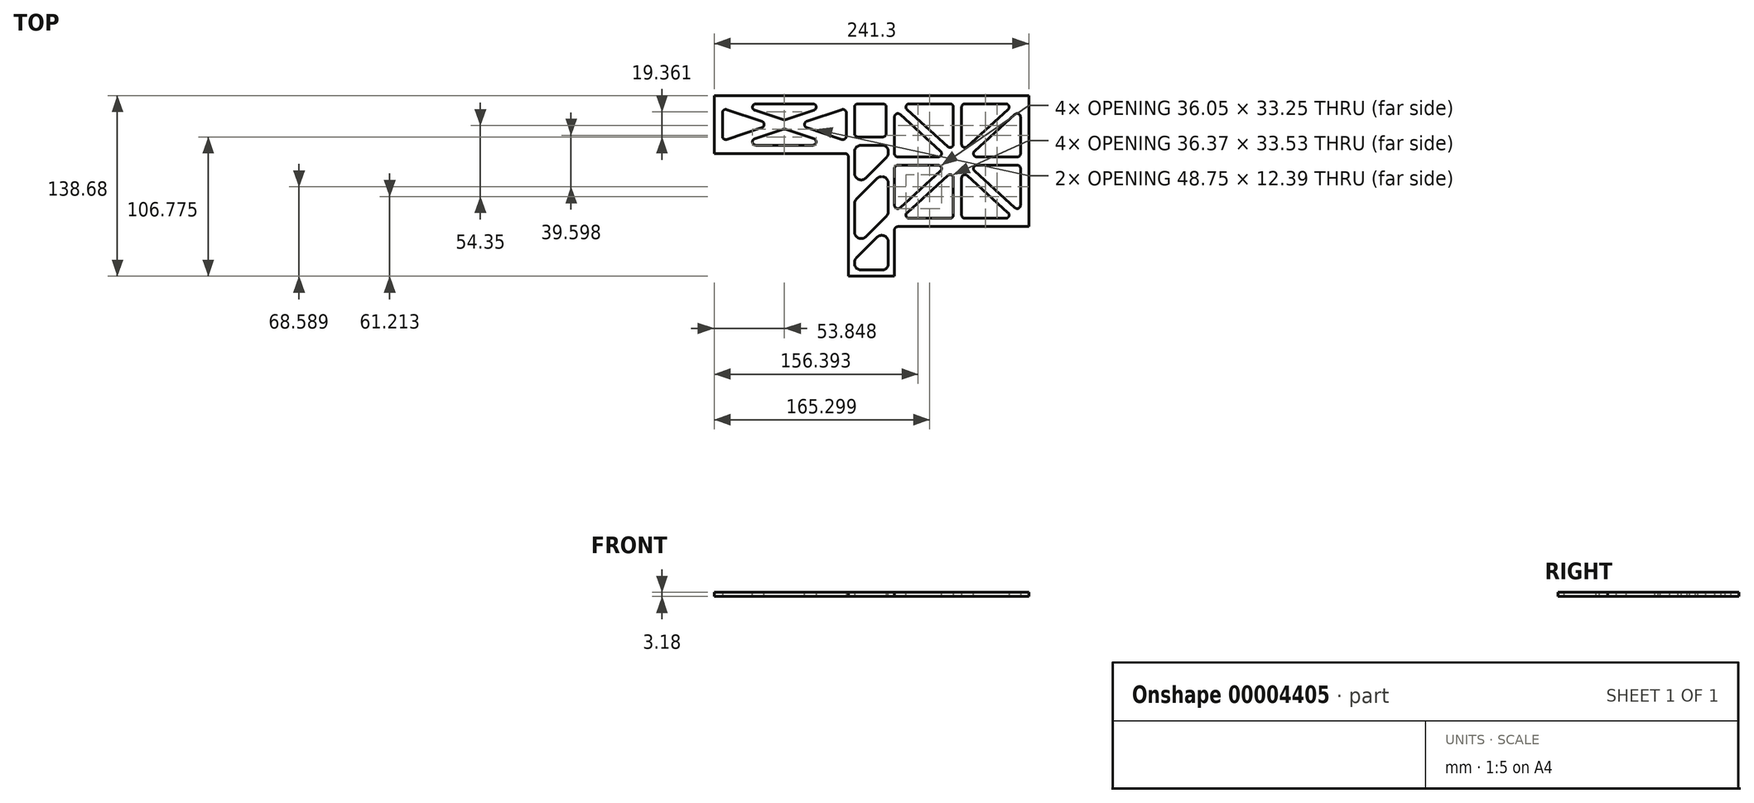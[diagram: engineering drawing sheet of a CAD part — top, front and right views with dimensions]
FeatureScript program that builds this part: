
annotation { "Feature Type Name" : "Feature", "Feature Type Description" : "" }
export const myFeature = defineFeature(function(context is Context, id is Id, definition is map)
    precondition{}
    {
        {
            var Q0;
            Q0=qCreatedBy(makeId("Top.planeOp"),FACE);
            var sketch = newSketch(context, id + "F0", { "sketchPlane" : qUnion([Q0])});
            skLineSegment(sketch, "E0", {"start": v(0, 0) * mm, "end": v(241.3, 0) * mm});
            skLineSegment(sketch, "E1", {"start": v(241.3, 0) * mm, "end": v(241.3, -100.58) * mm});
            skLineSegment(sketch, "E2", {"start": v(241.3, -100.58) * mm, "end": v(138.37, -100.58) * mm});
            skLineSegment(sketch, "E3", {"start": v(102.93, -44.45) * mm, "end": v(0, -44.45) * mm});
            skLineSegment(sketch, "E4", {"start": v(0, -44.45) * mm, "end": v(0, 0) * mm});
            skLineSegment(sketch, "E5.0", {"start": v(6.35, -34.75) * mm, "end": v(6.35, -9.7) * mm});
            skLineSegment(sketch, "E5.1", {"start": v(91.33, -38.1) * mm, "end": v(16.37, -38.1) * mm});
            skLineSegment(sketch, "E5.3", {"start": v(230.23, -94.23) * mm, "end": v(189.83, -94.23) * mm});
            skLineSegment(sketch, "E5.4", {"start": v(234.95, -10.64) * mm, "end": v(234.95, -47.12) * mm});
            skLineSegment(sketch, "E5.5", {"start": v(16.37, -6.35) * mm, "end": v(91.33, -6.35) * mm});
            skLineSegment(sketch, "E6", {"start": v(107.7, -31.75) * mm, "end": v(107.7, -6.35) * mm});
            skLineSegment(sketch, "E7.0", {"start": v(138.37, -89.94) * mm, "end": v(138.37, -53.47) * mm});
            skLineSegment(sketch, "E8.0", {"start": v(101.35, -34.75) * mm, "end": v(101.35, -9.7) * mm});
            skLineSegment(sketch, "E9.trimOffspring", {"start": v(143.08, -6.35) * mm, "end": v(183.48, -6.35) * mm});
            skLineSegment(sketch, "E10.trimOffspring", {"start": v(107.7, -6.35) * mm, "end": v(132.02, -6.35) * mm});
            skLineSegment(sketch, "E11.0", {"start": v(107.7, -31.75) * mm, "end": v(132.02, -31.75) * mm});
            skLineSegment(sketch, "E12.trimOffspring", {"start": v(132.02, -31.75) * mm, "end": v(132.02, -6.35) * mm});
            skLineSegment(sketch, "E13", {"start": v(234.95, -94.23) * mm, "end": v(138.37, -6.35) * mm, "construction": true});
            skLineSegment(sketch, "E14", {"start": v(138.37, -94.23) * mm, "end": v(234.95, -6.35) * mm, "construction": true});
            skLineSegment(sketch, "E15.0", {"start": v(234.95, -89.94) * mm, "end": v(194.87, -53.47) * mm});
            skLineSegment(sketch, "E16.0", {"start": v(230.23, -94.23) * mm, "end": v(189.83, -57.47) * mm});
            skLineSegment(sketch, "E17.0", {"start": v(143.08, -94.23) * mm, "end": v(183.48, -57.47) * mm});
            skLineSegment(sketch, "E18.0", {"start": v(138.37, -89.94) * mm, "end": v(178.45, -53.47) * mm});
            skLineSegment(sketch, "E19.trimOffspring", {"start": v(183.48, -43.11) * mm, "end": v(143.08, -6.35) * mm});
            skLineSegment(sketch, "E20.trimOffspring", {"start": v(194.87, -47.12) * mm, "end": v(234.95, -10.64) * mm});
            skLineSegment(sketch, "E21.trimOffspring", {"start": v(178.45, -47.12) * mm, "end": v(138.37, -10.64) * mm});
            skLineSegment(sketch, "E22.trimOffspring", {"start": v(189.83, -43.11) * mm, "end": v(230.23, -6.35) * mm});
            skLineSegment(sketch, "E23", {"start": v(234.95, -50.3) * mm, "end": v(138.37, -50.3) * mm, "construction": true});
            skLineSegment(sketch, "E24", {"start": v(186.66, -94.23) * mm, "end": v(186.66, -6.35) * mm, "construction": true});
            skLineSegment(sketch, "E25.0", {"start": v(189.83, -94.23) * mm, "end": v(189.83, -57.47) * mm});
            skLineSegment(sketch, "E26.0", {"start": v(183.48, -94.23) * mm, "end": v(183.48, -57.47) * mm});
            skLineSegment(sketch, "E27.0", {"start": v(234.95, -47.12) * mm, "end": v(194.87, -47.12) * mm});
            skLineSegment(sketch, "E28.0", {"start": v(234.95, -53.47) * mm, "end": v(194.87, -53.47) * mm});
            skLineSegment(sketch, "E29.trimOffspring", {"start": v(189.83, -43.11) * mm, "end": v(189.83, -6.35) * mm});
            skLineSegment(sketch, "E30.trimOffspring", {"start": v(183.48, -43.11) * mm, "end": v(183.48, -6.35) * mm});
            skLineSegment(sketch, "E31.trimOffspring", {"start": v(178.45, -47.12) * mm, "end": v(138.37, -47.12) * mm});
            skLineSegment(sketch, "E32.trimOffspring", {"start": v(178.45, -53.47) * mm, "end": v(138.37, -53.47) * mm});
            skLineSegment(sketch, "E33.trimOffspring", {"start": v(183.48, -94.23) * mm, "end": v(143.08, -94.23) * mm});
            skLineSegment(sketch, "E34.trimOffspring", {"start": v(138.37, -47.12) * mm, "end": v(138.37, -10.64) * mm});
            skLineSegment(sketch, "E35.trimOffspring", {"start": v(189.83, -6.35) * mm, "end": v(230.23, -6.35) * mm});
            skLineSegment(sketch, "E36.trimOffspring", {"start": v(234.95, -53.47) * mm, "end": v(234.95, -89.94) * mm});
            skLineSegment(sketch, "E37", {"start": v(101.35, -38.1) * mm, "end": v(6.35, -6.35) * mm, "construction": true});
            skLineSegment(sketch, "E38", {"start": v(6.35, -38.1) * mm, "end": v(101.35, -6.35) * mm, "construction": true});
            skLineSegment(sketch, "E39.0", {"start": v(101.35, -34.75) * mm, "end": v(63.86, -22.23) * mm});
            skLineSegment(sketch, "E40.0", {"start": v(91.33, -38.1) * mm, "end": v(53.85, -25.57) * mm});
            skLineSegment(sketch, "E41.0", {"start": v(16.37, -38.1) * mm, "end": v(53.85, -25.57) * mm});
            skLineSegment(sketch, "E42.0", {"start": v(6.35, -34.75) * mm, "end": v(43.83, -22.23) * mm});
            skLineSegment(sketch, "E43.trimOffspring", {"start": v(53.85, -18.88) * mm, "end": v(16.37, -6.35) * mm});
            skLineSegment(sketch, "E44.trimOffspring", {"start": v(63.86, -22.23) * mm, "end": v(101.35, -9.7) * mm});
            skLineSegment(sketch, "E45.trimOffspring", {"start": v(43.83, -22.23) * mm, "end": v(6.35, -9.7) * mm});
            skLineSegment(sketch, "E46.trimOffspring", {"start": v(53.85, -18.88) * mm, "end": v(91.33, -6.35) * mm});
            skLineSegment(sketch, "E47", {"start": v(138.37, -100.58) * mm, "end": v(138.37, -138.68) * mm});
            skLineSegment(sketch, "E48", {"start": v(138.37, -138.68) * mm, "end": v(102.93, -138.68) * mm});
            skLineSegment(sketch, "E49", {"start": v(102.93, -138.68) * mm, "end": v(102.93, -44.45) * mm});
            skSolve(sketch);
        }
        {
            var Q0;
            Q0=makeQuery(id+"F0.imprint","IMPRINT",FACE,{"disambiguationData":[TD([[makeQuery(id+"F0.imprint","IMPRINT",EDGE,{"derivedFrom":sQuery(id+"F0.wireOp",EDGE,"E0")}),-1.0]])]});
            extrude(context, id + "F1", {"entities" : qUnion([Q0]), "depth" : 3.17 * mm});
        }
        {
            var Q0;
            Q0=makeQuery(id+"F1.opExtrude","SWEPT_EDGE",EDGE,{"disambiguationData":[OSD([sQuery(id+"F0.wireOp",EDGE,"E3"),sQuery(id+"F0.wireOp",EDGE,"E49")])]});
            var Q1;
            Q1=makeQuery(id+"F1.opExtrude","SWEPT_EDGE",EDGE,{"disambiguationData":[OSD([sQuery(id+"F0.wireOp",EDGE,"E15.0"),sQuery(id+"F0.wireOp",EDGE,"E36.trimOffspring")])]});
            var Q2;
            Q2=makeQuery(id+"F1.opExtrude","SWEPT_EDGE",EDGE,{"disambiguationData":[OSD([sQuery(id+"F0.wireOp",EDGE,"E26.0"),sQuery(id+"F0.wireOp",EDGE,"E33.trimOffspring")])]});
            var Q3;
            Q3=makeQuery(id+"F1.opExtrude","SWEPT_EDGE",EDGE,{"disambiguationData":[OSD([sQuery(id+"F0.wireOp",EDGE,"E19.trimOffspring"),sQuery(id+"F0.wireOp",EDGE,"E30.trimOffspring")])]});
            var Q4;
            Q4=makeQuery(id+"F1.opExtrude","SWEPT_EDGE",EDGE,{"disambiguationData":[OSD([sQuery(id+"F0.wireOp",EDGE,"E5.4"),sQuery(id+"F0.wireOp",EDGE,"E27.0")])]});
            var Q5;
            Q5=makeQuery(id+"F1.opExtrude","SWEPT_EDGE",EDGE,{"disambiguationData":[OSD([sQuery(id+"F0.wireOp",EDGE,"E11.0"),sQuery(id+"F0.wireOp",EDGE,"E12.trimOffspring")])]});
            var Q6;
            Q6=makeQuery(id+"F1.opExtrude","SWEPT_EDGE",EDGE,{"disambiguationData":[OSD([sQuery(id+"F0.wireOp",EDGE,"E8.0"),sQuery(id+"F0.wireOp",EDGE,"E39.0")])]});
            var Q7;
            Q7=makeQuery(id+"F1.opExtrude","SWEPT_EDGE",EDGE,{"disambiguationData":[OSD([sQuery(id+"F0.wireOp",EDGE,"E43.trimOffspring"),sQuery(id+"F0.wireOp",EDGE,"E46.trimOffspring")])]});
            var Q8;
            Q8=makeQuery(id+"F1.opExtrude","SWEPT_EDGE",EDGE,{"disambiguationData":[OSD([sQuery(id+"F0.wireOp",EDGE,"E5.0"),sQuery(id+"F0.wireOp",EDGE,"E45.trimOffspring")])]});
            var Q9;
            Q9=makeQuery(id+"F1.opExtrude","SWEPT_EDGE",EDGE,{"disambiguationData":[OSD([sQuery(id+"F0.wireOp",EDGE,"E40.0"),sQuery(id+"F0.wireOp",EDGE,"E41.0")])]});
            var Q10;
            Q10=makeQuery(id+"F1.opExtrude","SWEPT_EDGE",EDGE,{"disambiguationData":[OSD([sQuery(id+"F0.wireOp",EDGE,"E6"),sQuery(id+"F0.wireOp",EDGE,"E10.trimOffspring")])]});
            var Q11;
            Q11=makeQuery(id+"F1.opExtrude","SWEPT_EDGE",EDGE,{"disambiguationData":[OSD([sQuery(id+"F0.wireOp",EDGE,"E9.trimOffspring"),sQuery(id+"F0.wireOp",EDGE,"E19.trimOffspring")])]});
            var Q12;
            Q12=makeQuery(id+"F1.opExtrude","SWEPT_EDGE",EDGE,{"disambiguationData":[OSD([sQuery(id+"F0.wireOp",EDGE,"E29.trimOffspring"),sQuery(id+"F0.wireOp",EDGE,"E35.trimOffspring")])]});
            var Q13;
            Q13=makeQuery(id+"F1.opExtrude","SWEPT_EDGE",EDGE,{"disambiguationData":[OSD([sQuery(id+"F0.wireOp",EDGE,"E15.0"),sQuery(id+"F0.wireOp",EDGE,"E28.0")])]});
            var Q14;
            Q14=makeQuery(id+"F1.opExtrude","SWEPT_EDGE",EDGE,{"disambiguationData":[OSD([sQuery(id+"F0.wireOp",EDGE,"E7.0"),sQuery(id+"F0.wireOp",EDGE,"E32.trimOffspring")])]});
            var Q15;
            Q15=makeQuery(id+"F1.opExtrude","SWEPT_EDGE",EDGE,{"disambiguationData":[OSD([sQuery(id+"F0.wireOp",EDGE,"E39.0"),sQuery(id+"F0.wireOp",EDGE,"E44.trimOffspring")])]});
            var Q16;
            Q16=makeQuery(id+"F1.opExtrude","SWEPT_EDGE",EDGE,{"disambiguationData":[OSD([sQuery(id+"F0.wireOp",EDGE,"E31.trimOffspring"),sQuery(id+"F0.wireOp",EDGE,"E34.trimOffspring")])]});
            var Q17;
            Q17=makeQuery(id+"F1.opExtrude","SWEPT_EDGE",EDGE,{"disambiguationData":[OSD([sQuery(id+"F0.wireOp",EDGE,"E20.trimOffspring"),sQuery(id+"F0.wireOp",EDGE,"E27.0")])]});
            var Q18;
            Q18=makeQuery(id+"F1.opExtrude","SWEPT_EDGE",EDGE,{"disambiguationData":[OSD([sQuery(id+"F0.wireOp",EDGE,"E17.0"),sQuery(id+"F0.wireOp",EDGE,"E33.trimOffspring")])]});
            var Q19;
            Q19=makeQuery(id+"F1.opExtrude","SWEPT_EDGE",EDGE,{"disambiguationData":[OSD([sQuery(id+"F0.wireOp",EDGE,"E5.3"),sQuery(id+"F0.wireOp",EDGE,"E25.0")])]});
            var Q20;
            Q20=makeQuery(id+"F1.opExtrude","SWEPT_EDGE",EDGE,{"disambiguationData":[OSD([sQuery(id+"F0.wireOp",EDGE,"E6"),sQuery(id+"F0.wireOp",EDGE,"E11.0")])]});
            var Q21;
            Q21=makeQuery(id+"F1.opExtrude","SWEPT_EDGE",EDGE,{"disambiguationData":[OSD([sQuery(id+"F0.wireOp",EDGE,"E5.1"),sQuery(id+"F0.wireOp",EDGE,"E41.0")])]});
            var Q22;
            Q22=makeQuery(id+"F1.opExtrude","SWEPT_EDGE",EDGE,{"disambiguationData":[OSD([sQuery(id+"F0.wireOp",EDGE,"E5.0"),sQuery(id+"F0.wireOp",EDGE,"E42.0")])]});
            var Q23;
            Q23=makeQuery(id+"F1.opExtrude","SWEPT_EDGE",EDGE,{"disambiguationData":[OSD([sQuery(id+"F0.wireOp",EDGE,"E7.0"),sQuery(id+"F0.wireOp",EDGE,"E18.0")])]});
            var Q24;
            Q24=makeQuery(id+"F1.opExtrude","SWEPT_EDGE",EDGE,{"disambiguationData":[OSD([sQuery(id+"F0.wireOp",EDGE,"E22.trimOffspring"),sQuery(id+"F0.wireOp",EDGE,"E29.trimOffspring")])]});
            var Q25;
            Q25=makeQuery(id+"F1.opExtrude","SWEPT_EDGE",EDGE,{"disambiguationData":[OSD([sQuery(id+"F0.wireOp",EDGE,"E8.0"),sQuery(id+"F0.wireOp",EDGE,"E44.trimOffspring")])]});
            var Q26;
            Q26=makeQuery(id+"F1.opExtrude","SWEPT_EDGE",EDGE,{"disambiguationData":[OSD([sQuery(id+"F0.wireOp",EDGE,"E10.trimOffspring"),sQuery(id+"F0.wireOp",EDGE,"E12.trimOffspring")])]});
            var Q27;
            Q27=makeQuery(id+"F1.opExtrude","SWEPT_EDGE",EDGE,{"disambiguationData":[OSD([sQuery(id+"F0.wireOp",EDGE,"E5.4"),sQuery(id+"F0.wireOp",EDGE,"E20.trimOffspring")])]});
            var Q28;
            Q28=makeQuery(id+"F1.opExtrude","SWEPT_EDGE",EDGE,{"disambiguationData":[OSD([sQuery(id+"F0.wireOp",EDGE,"E17.0"),sQuery(id+"F0.wireOp",EDGE,"E26.0")])]});
            var Q29;
            Q29=makeQuery(id+"F1.opExtrude","SWEPT_EDGE",EDGE,{"disambiguationData":[OSD([sQuery(id+"F0.wireOp",EDGE,"E16.0"),sQuery(id+"F0.wireOp",EDGE,"E25.0")])]});
            var Q30;
            Q30=makeQuery(id+"F1.opExtrude","SWEPT_EDGE",EDGE,{"disambiguationData":[OSD([sQuery(id+"F0.wireOp",EDGE,"E21.trimOffspring"),sQuery(id+"F0.wireOp",EDGE,"E34.trimOffspring")])]});
            var Q31;
            Q31=makeQuery(id+"F1.opExtrude","SWEPT_EDGE",EDGE,{"disambiguationData":[OSD([sQuery(id+"F0.wireOp",EDGE,"E5.5"),sQuery(id+"F0.wireOp",EDGE,"E43.trimOffspring")])]});
            var Q32;
            Q32=makeQuery(id+"F1.opExtrude","SWEPT_EDGE",EDGE,{"disambiguationData":[OSD([sQuery(id+"F0.wireOp",EDGE,"E42.0"),sQuery(id+"F0.wireOp",EDGE,"E45.trimOffspring")])]});
            var Q33;
            Q33=makeQuery(id+"F1.opExtrude","SWEPT_EDGE",EDGE,{"disambiguationData":[OSD([sQuery(id+"F0.wireOp",EDGE,"E5.5"),sQuery(id+"F0.wireOp",EDGE,"E46.trimOffspring")])]});
            var Q34;
            Q34=makeQuery(id+"F1.opExtrude","SWEPT_EDGE",EDGE,{"disambiguationData":[OSD([sQuery(id+"F0.wireOp",EDGE,"E22.trimOffspring"),sQuery(id+"F0.wireOp",EDGE,"E35.trimOffspring")])]});
            var Q35;
            Q35=makeQuery(id+"F1.opExtrude","SWEPT_EDGE",EDGE,{"disambiguationData":[OSD([sQuery(id+"F0.wireOp",EDGE,"E9.trimOffspring"),sQuery(id+"F0.wireOp",EDGE,"E30.trimOffspring")])]});
            var Q36;
            Q36=makeQuery(id+"F1.opExtrude","SWEPT_EDGE",EDGE,{"disambiguationData":[OSD([sQuery(id+"F0.wireOp",EDGE,"E21.trimOffspring"),sQuery(id+"F0.wireOp",EDGE,"E31.trimOffspring")])]});
            var Q37;
            Q37=makeQuery(id+"F1.opExtrude","SWEPT_EDGE",EDGE,{"disambiguationData":[OSD([sQuery(id+"F0.wireOp",EDGE,"E5.3"),sQuery(id+"F0.wireOp",EDGE,"E16.0")])]});
            var Q38;
            Q38=makeQuery(id+"F1.opExtrude","SWEPT_EDGE",EDGE,{"disambiguationData":[OSD([sQuery(id+"F0.wireOp",EDGE,"E5.1"),sQuery(id+"F0.wireOp",EDGE,"E40.0")])]});
            var Q39;
            Q39=makeQuery(id+"F1.opExtrude","SWEPT_EDGE",EDGE,{"disambiguationData":[OSD([sQuery(id+"F0.wireOp",EDGE,"E18.0"),sQuery(id+"F0.wireOp",EDGE,"E32.trimOffspring")])]});
            var Q40;
            Q40=makeQuery(id+"F1.opExtrude","SWEPT_EDGE",EDGE,{"disambiguationData":[OSD([sQuery(id+"F0.wireOp",EDGE,"E28.0"),sQuery(id+"F0.wireOp",EDGE,"E36.trimOffspring")])]});
            var Q41;
            Q41=makeQuery(id+"F1.opExtrude","SWEPT_EDGE",EDGE,{"disambiguationData":[OSD([sQuery(id+"F0.wireOp",EDGE,"E2"),sQuery(id+"F0.wireOp",EDGE,"E47")])]});
            fillet(context, id + "F2", {"entities" : qUnion([Q0, Q1, Q2, Q3, Q4, Q5, Q6, Q7, Q8, Q9, Q10, Q11, Q12, Q13, Q14, Q15, Q16, Q17, Q18, Q19, Q20, Q21, Q22, Q23, Q24, Q25, Q26, Q27, Q28, Q29, Q30, Q31, Q32, Q33, Q34, Q35, Q36, Q37, Q38, Q39, Q40, Q41]), "radius" : 2.54 * mm, "tangentPropagation" : true, "allowEdgeOverflow" : false});
        }
        {
            var Q0;
            Q0=makeQuery(id+"F1.opExtrude","CAP_FACE",FACE,{"disambiguationData":[OSD([sQuery(id+"F0.wireOp",EDGE,"E0"),sQuery(id+"F0.wireOp",EDGE,"E1"),sQuery(id+"F0.wireOp",EDGE,"E2"),sQuery(id+"F0.wireOp",EDGE,"E3"),sQuery(id+"F0.wireOp",EDGE,"E4"),sQuery(id+"F0.wireOp",EDGE,"E5.0"),sQuery(id+"F0.wireOp",EDGE,"E5.1"),sQuery(id+"F0.wireOp",EDGE,"E5.3"),sQuery(id+"F0.wireOp",EDGE,"E5.4"),sQuery(id+"F0.wireOp",EDGE,"E5.5"),sQuery(id+"F0.wireOp",EDGE,"E6"),sQuery(id+"F0.wireOp",EDGE,"E7.0"),sQuery(id+"F0.wireOp",EDGE,"E8.0"),sQuery(id+"F0.wireOp",EDGE,"E9.trimOffspring"),sQuery(id+"F0.wireOp",EDGE,"E10.trimOffspring"),sQuery(id+"F0.wireOp",EDGE,"E11.0"),sQuery(id+"F0.wireOp",EDGE,"E12.trimOffspring"),sQuery(id+"F0.wireOp",EDGE,"E15.0"),sQuery(id+"F0.wireOp",EDGE,"E16.0"),sQuery(id+"F0.wireOp",EDGE,"E17.0"),sQuery(id+"F0.wireOp",EDGE,"E18.0"),sQuery(id+"F0.wireOp",EDGE,"E19.trimOffspring"),sQuery(id+"F0.wireOp",EDGE,"E20.trimOffspring"),sQuery(id+"F0.wireOp",EDGE,"E21.trimOffspring"),sQuery(id+"F0.wireOp",EDGE,"E22.trimOffspring"),sQuery(id+"F0.wireOp",EDGE,"E25.0"),sQuery(id+"F0.wireOp",EDGE,"E26.0"),sQuery(id+"F0.wireOp",EDGE,"E27.0"),sQuery(id+"F0.wireOp",EDGE,"E28.0"),sQuery(id+"F0.wireOp",EDGE,"E29.trimOffspring"),sQuery(id+"F0.wireOp",EDGE,"E30.trimOffspring"),sQuery(id+"F0.wireOp",EDGE,"E31.trimOffspring"),sQuery(id+"F0.wireOp",EDGE,"E32.trimOffspring"),sQuery(id+"F0.wireOp",EDGE,"E33.trimOffspring"),sQuery(id+"F0.wireOp",EDGE,"E34.trimOffspring"),sQuery(id+"F0.wireOp",EDGE,"E35.trimOffspring"),sQuery(id+"F0.wireOp",EDGE,"E36.trimOffspring"),sQuery(id+"F0.wireOp",EDGE,"E39.0"),sQuery(id+"F0.wireOp",EDGE,"E40.0"),sQuery(id+"F0.wireOp",EDGE,"E41.0"),sQuery(id+"F0.wireOp",EDGE,"E42.0"),sQuery(id+"F0.wireOp",EDGE,"E43.trimOffspring"),sQuery(id+"F0.wireOp",EDGE,"E44.trimOffspring"),sQuery(id+"F0.wireOp",EDGE,"E45.trimOffspring"),sQuery(id+"F0.wireOp",EDGE,"E46.trimOffspring"),sQuery(id+"F0.wireOp",EDGE,"E47"),sQuery(id+"F0.wireOp",EDGE,"E48"),sQuery(id+"F0.wireOp",EDGE,"E49")])],"isStart":false});
            var sketch = newSketch(context, id + "F3", { "sketchPlane" : qUnion([Q0])});
            skLineSegment(sketch, "E50.bottom", {"start": v(107.7, -38.1) * mm, "end": v(133.6, -38.1) * mm});
            skLineSegment(sketch, "E50.top", {"start": v(107.7, -133.92) * mm, "end": v(133.6, -133.92) * mm});
            skLineSegment(sketch, "E50.left", {"start": v(107.7, -38.1) * mm, "end": v(107.7, -71.95) * mm});
            skLineSegment(sketch, "E50.right", {"start": v(133.6, -38.1) * mm, "end": v(133.6, -46.04) * mm});
            skLineSegment(sketch, "E51", {"start": v(107.7, -71.95) * mm, "end": v(133.6, -46.04) * mm});
            skLineSegment(sketch, "E52", {"start": v(107.7, -80.93) * mm, "end": v(133.6, -55.02) * mm});
            skLineSegment(sketch, "E53.trimOffspring", {"start": v(107.7, -80.93) * mm, "end": v(107.7, -117) * mm});
            skLineSegment(sketch, "E54.trimOffspring", {"start": v(133.6, -55.02) * mm, "end": v(133.6, -91.1) * mm});
            skLineSegment(sketch, "E55", {"start": v(107.7, -117) * mm, "end": v(133.6, -91.1) * mm});
            skLineSegment(sketch, "E56", {"start": v(107.7, -125.98) * mm, "end": v(133.6, -100.08) * mm});
            skLineSegment(sketch, "E57.trimOffspring", {"start": v(107.7, -125.98) * mm, "end": v(107.7, -133.92) * mm});
            skLineSegment(sketch, "E58.trimOffspring", {"start": v(133.6, -100.08) * mm, "end": v(133.6, -133.92) * mm});
            skSolve(sketch);
        }
        {
            var Q0;
            Q0 = qSketchRegion(id + "F3", true);
            extrude(context, id + "F4", {"entities" : qUnion([Q0]), "operationType" : NewBodyOperationType.REMOVE, "endBound" : BoundingType.THROUGH_ALL, "oppositeDirection" : true, "depth" : 25.4 * mm});
        }
        {
            var Q0;
            Q0=makeQuery(id+"F4.boolean.opBoolean","COPY",EDGE,{"derivedFrom":makeQuery(id+"F4.opExtrude","SWEPT_EDGE",EDGE,{"disambiguationData":[OSD([sQuery(id+"F3.wireOp",EDGE,"E50.bottom"),sQuery(id+"F3.wireOp",EDGE,"E50.left")])]})});
            var Q1;
            Q1=makeQuery(id+"F4.boolean.opBoolean","COPY",EDGE,{"derivedFrom":makeQuery(id+"F4.opExtrude","SWEPT_EDGE",EDGE,{"disambiguationData":[OSD([sQuery(id+"F3.wireOp",EDGE,"E52"),sQuery(id+"F3.wireOp",EDGE,"E53.trimOffspring")])]})});
            var Q2;
            Q2=makeQuery(id+"F4.boolean.opBoolean","COPY",EDGE,{"derivedFrom":makeQuery(id+"F4.opExtrude","SWEPT_EDGE",EDGE,{"disambiguationData":[OSD([sQuery(id+"F3.wireOp",EDGE,"E56"),sQuery(id+"F3.wireOp",EDGE,"E57.trimOffspring")])]})});
            var Q3;
            Q3=makeQuery(id+"F4.boolean.opBoolean","COPY",EDGE,{"derivedFrom":makeQuery(id+"F4.opExtrude","SWEPT_EDGE",EDGE,{"disambiguationData":[OSD([sQuery(id+"F3.wireOp",EDGE,"E50.bottom"),sQuery(id+"F3.wireOp",EDGE,"E50.right")])]})});
            var Q4;
            Q4=makeQuery(id+"F4.boolean.opBoolean","COPY",EDGE,{"derivedFrom":makeQuery(id+"F4.opExtrude","SWEPT_EDGE",EDGE,{"disambiguationData":[OSD([sQuery(id+"F3.wireOp",EDGE,"E52"),sQuery(id+"F3.wireOp",EDGE,"E54.trimOffspring")])]})});
            var Q5;
            Q5=makeQuery(id+"F4.boolean.opBoolean","COPY",EDGE,{"derivedFrom":makeQuery(id+"F4.opExtrude","SWEPT_EDGE",EDGE,{"disambiguationData":[OSD([sQuery(id+"F3.wireOp",EDGE,"E56"),sQuery(id+"F3.wireOp",EDGE,"E58.trimOffspring")])]})});
            var Q6;
            Q6=makeQuery(id+"F4.boolean.opBoolean","COPY",EDGE,{"derivedFrom":makeQuery(id+"F4.opExtrude","SWEPT_EDGE",EDGE,{"disambiguationData":[OSD([sQuery(id+"F3.wireOp",EDGE,"E50.right"),sQuery(id+"F3.wireOp",EDGE,"E51")])]})});
            var Q7;
            Q7=makeQuery(id+"F4.boolean.opBoolean","COPY",EDGE,{"derivedFrom":makeQuery(id+"F4.opExtrude","SWEPT_EDGE",EDGE,{"disambiguationData":[OSD([sQuery(id+"F3.wireOp",EDGE,"E54.trimOffspring"),sQuery(id+"F3.wireOp",EDGE,"E55")])]})});
            var Q8;
            Q8=makeQuery(id+"F4.boolean.opBoolean","COPY",EDGE,{"derivedFrom":makeQuery(id+"F4.opExtrude","SWEPT_EDGE",EDGE,{"disambiguationData":[OSD([sQuery(id+"F3.wireOp",EDGE,"E50.top"),sQuery(id+"F3.wireOp",EDGE,"E58.trimOffspring")])]})});
            var Q9;
            Q9=makeQuery(id+"F4.boolean.opBoolean","COPY",EDGE,{"derivedFrom":makeQuery(id+"F4.opExtrude","SWEPT_EDGE",EDGE,{"disambiguationData":[OSD([sQuery(id+"F3.wireOp",EDGE,"E50.left"),sQuery(id+"F3.wireOp",EDGE,"E51")])]})});
            var Q10;
            Q10=makeQuery(id+"F4.boolean.opBoolean","COPY",EDGE,{"derivedFrom":makeQuery(id+"F4.opExtrude","SWEPT_EDGE",EDGE,{"disambiguationData":[OSD([sQuery(id+"F3.wireOp",EDGE,"E53.trimOffspring"),sQuery(id+"F3.wireOp",EDGE,"E55")])]})});
            var Q11;
            Q11=makeQuery(id+"F4.boolean.opBoolean","COPY",EDGE,{"derivedFrom":makeQuery(id+"F4.opExtrude","SWEPT_EDGE",EDGE,{"disambiguationData":[OSD([sQuery(id+"F3.wireOp",EDGE,"E50.top"),sQuery(id+"F3.wireOp",EDGE,"E57.trimOffspring")])]})});
            fillet(context, id + "F5", {"entities" : qUnion([Q0, Q1, Q2, Q3, Q4, Q5, Q6, Q7, Q8, Q9, Q10, Q11]), "radius" : 5.08 * mm, "tangentPropagation" : true, "allowEdgeOverflow" : false});
        }
    });
